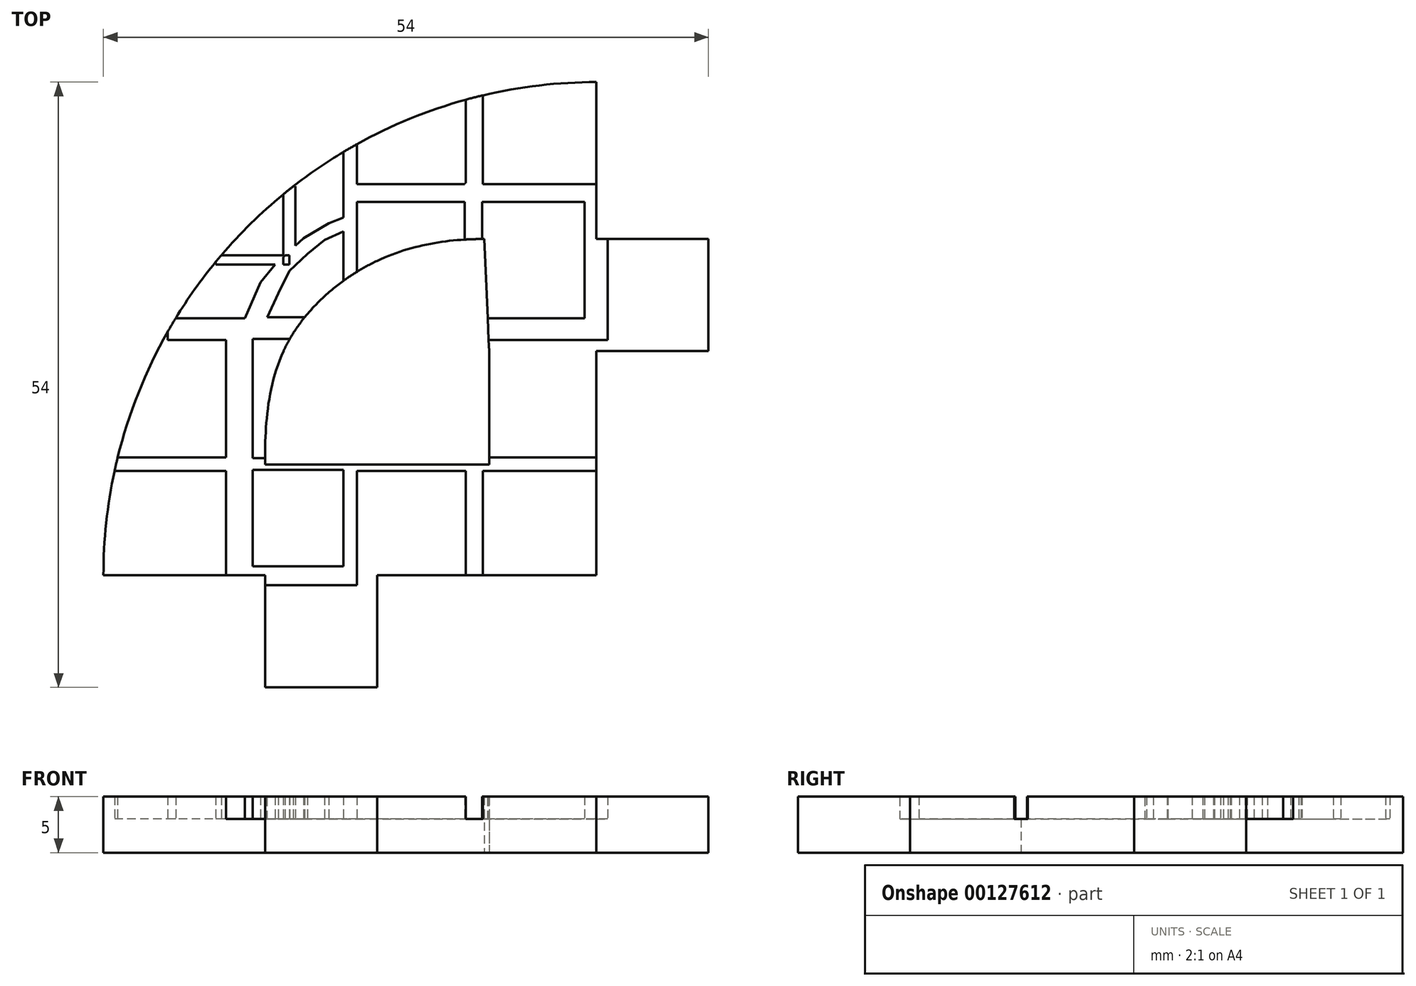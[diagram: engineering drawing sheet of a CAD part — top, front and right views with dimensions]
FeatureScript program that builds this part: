
annotation { "Feature Type Name" : "Feature", "Feature Type Description" : "" }
export const myFeature = defineFeature(function(context is Context, id is Id, definition is map)
    precondition{}
    {
        {
            var Q0;
            Q0=qCreatedBy(makeId("Top.planeOp"),FACE);
            cPlane(context, id + "F0", {"entities" : qUnion([Q0]), "cplaneType" : CPlaneType.OFFSET, "offset" : 3 * mm, "width" : 150 * mm, "height" : 150 * mm});
        }
        {
            var Q0;
            Q0=qCreatedBy(makeId("Top.planeOp"),FACE);
            var sketch = newSketch(context, id + "F1", { "sketchPlane" : qUnion([Q0])});
            skLineSegment(sketch, "E0", {"start": v(0, 0) * mm, "end": v(-19.58, 0) * mm});
            skLineSegment(sketch, "E1", {"start": v(0, 0) * mm, "end": v(0, 20) * mm});
            skLineSegment(sketch, "E2.bottom", {"start": v(0, 0) * mm, "end": v(-10, 0) * mm});
            skLineSegment(sketch, "E2.top", {"start": v(0, 9.9) * mm, "end": v(-9.58, 9.9) * mm});
            skLineSegment(sketch, "E3.bottom", {"start": v(-9.58, 9.9) * mm, "end": v(0.42, 9.9) * mm});
            skLineSegment(sketch, "E3.top", {"start": v(-9.58, 20) * mm, "end": v(0, 20) * mm});
            skLineSegment(sketch, "E3.left", {"start": v(-9.58, 9.9) * mm, "end": v(-9.58, 20) * mm});
            skLineSegment(sketch, "E4.bottom", {"start": v(-9.58, 20) * mm, "end": v(0.42, 20) * mm});
            skLineSegment(sketch, "E5.bottom", {"start": v(-9.58, 9.9) * mm, "end": v(-19.58, 9.9) * mm});
            skLineSegment(sketch, "E5.top", {"start": v(-9.58, 0) * mm, "end": v(-19.58, 0) * mm});
            skLineSegment(sketch, "E5.left", {"start": v(-9.58, 9.9) * mm, "end": v(-9.58, 0) * mm});
            skLineSegment(sketch, "E5.right", {"start": v(-19.58, 9.9) * mm, "end": v(-19.58, 0) * mm});
            skLineSegment(sketch, "E6.right", {"start": v(-29.58, 9.9) * mm, "end": v(-29.58, 0) * mm});
            skLineSegment(sketch, "E7.bottom", {"start": v(-29.58, 9.9) * mm, "end": v(-42.6, 9.9) * mm});
            skLineSegment(sketch, "E8.bottom", {"start": v(-10, 30) * mm, "end": v(0, 30) * mm});
            skLineSegment(sketch, "E9.left", {"start": v(-29.58, 0) * mm, "end": v(-29.58, -10) * mm});
            skLineSegment(sketch, "E9.right", {"start": v(-19.58, 0) * mm, "end": v(-19.58, -10) * mm});
            skLineSegment(sketch, "E10.bottom", {"start": v(0, 20) * mm, "end": v(10, 20) * mm});
            skLineSegment(sketch, "E10.top", {"start": v(0, 30) * mm, "end": v(10, 30) * mm});
            skArc(sketch, "E11", {"start": v(0, 44) * mm, "mid": v(-31.11, 31.11) * mm, "end": v(-44, 0) * mm});
            skLineSegment(sketch, "E12", {"start": v(-10, 30) * mm, "end": v(-10, 42.85) * mm});
            skLineSegment(sketch, "E13", {"start": v(-29.58, -10) * mm, "end": v(-19.58, -10) * mm});
            skLineSegment(sketch, "E14", {"start": v(-29.58, 0) * mm, "end": v(-19.58, 0) * mm});
            skLineSegment(sketch, "E15", {"start": v(-29.58, 9.9) * mm, "end": v(-19.58, 9.9) * mm});
            skLineSegment(sketch, "E16", {"start": v(0, 0) * mm, "end": v(0, 9.9) * mm});
            skLineSegment(sketch, "E17", {"start": v(-9.58, 20) * mm, "end": v(-10, 30) * mm});
            skLineSegment(sketch, "E18", {"start": v(0, 30) * mm, "end": v(0, 20) * mm});
            skLineSegment(sketch, "E19", {"start": v(10, 30) * mm, "end": v(10, 20) * mm});
            skFitSpline(sketch, "E20", {"points": [v(-29.58, 9.9) * mm, v(-27.93, 20) * mm, v(-19.58, 28.05) * mm, v(-10, 30) * mm], "startDerivative": vector(-0.16, 25.5) * mm, "endDerivative": vector(29.05, 0) * mm});
            skLineSegment(sketch, "E21", {"start": v(-19.58, 9.9) * mm, "end": v(-19.58, 28.05) * mm});
            skLineSegment(sketch, "E22", {"start": v(-9.58, 20) * mm, "end": v(-27.93, 20) * mm});
            skLineSegment(sketch, "E23", {"start": v(-27.93, 20) * mm, "end": v(-39.2, 20) * mm});
            skLineSegment(sketch, "E24", {"start": v(-19.58, 28.05) * mm, "end": v(-19.58, 39.4) * mm});
            skLineSegment(sketch, "E25", {"start": v(0, 44) * mm, "end": v(0, 30) * mm});
            skLineSegment(sketch, "E26", {"start": v(-44, 0) * mm, "end": v(-29.58, 0) * mm});
            skLineSegment(sketch, "E27", {"start": v(-33.93, 28) * mm, "end": v(-24.58, 24.6) * mm});
            skPoint(sketch, "E27.endSnap0", {"position": v(-24.58, 0) * mm});
            skLineSegment(sketch, "E28", {"start": v(-24.58, 24.6) * mm, "end": v(-27.98, 33.96) * mm});
            skLineSegment(sketch, "E29", {"start": v(-29.58, 9.9) * mm, "end": v(-24.58, 24.6) * mm, "construction": true});
            skLineSegment(sketch, "E30", {"start": v(-10, 30) * mm, "end": v(-24.58, 24.6) * mm, "construction": true});
            skSolve(sketch);
        }
        {
            var Q0;
            Q0 = qSketchRegion(id + "F1", true);
            var Q1;
            {var subQ0=sQuery(id+"F1.wireOp",EDGE,"ekZmYGLB-jqZX-6x8J-CA2y-MRHvwaimWM1N.bottom");Q1=makeQuery(id+"F1.imprint","IMPRINT",FACE,{"disambiguationData":[TD([[makeQuery(id+"F1.imprint","IMPRINT",EDGE,{"derivedFrom":subQ0}),1.0]])]});}
            var Q2;
            Q2=makeQuery(id+"F1.imprint","IMPRINT",FACE,{"disambiguationData":[TD([[makeQuery(id+"F1.imprint","IMPRINT",EDGE,{"derivedFrom":sQuery(id+"F1.wireOp",EDGE,"LGzSSFG5-AHb3-na1S-sf8x-pvlMwqtWAyyH.bottom")}),1.0]])]});
            var Q3;
            Q3=makeQuery(id+"F1.imprint","IMPRINT",FACE,{"disambiguationData":[TD([[makeQuery(id+"F1.imprint","IMPRINT",EDGE,{"derivedFrom":sQuery(id+"F1.wireOp",EDGE,"sXpVq7aK-24pz-09u2-ev60-LyjVWQO6ttF5.bottom")}),1.0]])]});
            var Q4;
            Q4=makeQuery(id+"F1.imprint","IMPRINT",FACE,{"disambiguationData":[TD([[makeQuery(id+"F1.imprint","IMPRINT",EDGE,{"derivedFrom":sQuery(id+"F1.wireOp",EDGE,"ivGXcJoi-03Uq-7aqn-IO81-W6c1Jl31SRKL.bottom")}),1.0]])]});
            extrude(context, id + "F2", {"entities" : qUnion([Q0, Q1, Q2, Q3, Q4]), "depth" : 5 * mm});
        }
        {
            var Q0;
            Q0=qCreatedBy(id+"F0.planeOp",FACE);
            var sketch = newSketch(context, id + "F3", { "sketchPlane" : qUnion([Q0])});
            skLineSegment(sketch, "E31", {"start": v(-33.07, 0) * mm, "end": v(-33.07, 22.94) * mm});
            skLineSegment(sketch, "E32", {"start": v(-33.07, 22.94) * mm, "end": v(-30.69, 22.94) * mm});
            skLineSegment(sketch, "E33", {"start": v(-30.69, 22.94) * mm, "end": v(-30.69, 0) * mm});
            skLineSegment(sketch, "E34", {"start": v(-30.69, 0) * mm, "end": v(-33.07, 0) * mm});
            skLineSegment(sketch, "E35.bottom", {"start": v(-22.58, 0) * mm, "end": v(-21.39, 0) * mm});
            skLineSegment(sketch, "E35.top", {"start": v(-22.58, 38.74) * mm, "end": v(-21.39, 38.74) * mm});
            skLineSegment(sketch, "E35.left", {"start": v(-22.58, 0) * mm, "end": v(-22.58, 38.74) * mm});
            skLineSegment(sketch, "E35.right", {"start": v(-21.39, 0) * mm, "end": v(-21.39, 38.74) * mm});
            skLineSegment(sketch, "E36.bottom", {"start": v(-11.65, 0) * mm, "end": v(-10.13, 0) * mm});
            skLineSegment(sketch, "E36.top", {"start": v(-11.65, 43.5) * mm, "end": v(-10.13, 43.5) * mm});
            skLineSegment(sketch, "E36.left", {"start": v(-11.65, 0) * mm, "end": v(-11.65, 43.5) * mm});
            skLineSegment(sketch, "E36.right", {"start": v(-10.13, 0) * mm, "end": v(-10.13, 43.5) * mm});
            skLineSegment(sketch, "E37.bottom", {"start": v(0, 9.3) * mm, "end": v(-43.24, 9.3) * mm});
            skLineSegment(sketch, "E37.top", {"start": v(0, 10.5) * mm, "end": v(-43.24, 10.5) * mm});
            skLineSegment(sketch, "E37.left", {"start": v(0, 9.3) * mm, "end": v(0, 10.5) * mm});
            skLineSegment(sketch, "E37.right", {"start": v(-43.24, 9.3) * mm, "end": v(-43.24, 10.5) * mm});
            skPoint(sketch, "E38.oppositeSnap0", {"position": v(-31.88, 22.94) * mm});
            skLineSegment(sketch, "E38.bottom", {"start": v(0, 21) * mm, "end": v(-38.26, 21) * mm});
            skLineSegment(sketch, "E38.top", {"start": v(0, 22.94) * mm, "end": v(-38.26, 22.94) * mm});
            skLineSegment(sketch, "E38.left", {"start": v(0, 21) * mm, "end": v(0, 22.94) * mm});
            skLineSegment(sketch, "E38.right", {"start": v(-38.26, 21) * mm, "end": v(-38.26, 22.94) * mm});
            skLineSegment(sketch, "E39.bottom", {"start": v(-1.04, 22.94) * mm, "end": v(1.01, 22.94) * mm});
            skLineSegment(sketch, "E39.top", {"start": v(-1.04, 34.2) * mm, "end": v(1.01, 34.2) * mm});
            skLineSegment(sketch, "E39.left", {"start": v(-1.04, 22.94) * mm, "end": v(-1.04, 34.2) * mm});
            skLineSegment(sketch, "E39.right", {"start": v(1.01, 22.94) * mm, "end": v(1.01, 34.2) * mm});
            skLineSegment(sketch, "E40.bottom", {"start": v(1.01, 22.94) * mm, "end": v(-1.04, 22.94) * mm});
            skLineSegment(sketch, "E40.top", {"start": v(1.01, 21) * mm, "end": v(-1.04, 21) * mm});
            skLineSegment(sketch, "E40.left", {"start": v(1.01, 22.94) * mm, "end": v(1.01, 21) * mm});
            skLineSegment(sketch, "E40.right", {"start": v(-1.04, 22.94) * mm, "end": v(-1.04, 21) * mm});
            skPoint(sketch, "E41.oppositeSnap0", {"position": v(-0.02, 34.2) * mm});
            skLineSegment(sketch, "E41.bottom", {"start": v(-22.58, 34.9) * mm, "end": v(-0.02, 34.9) * mm});
            skLineSegment(sketch, "E41.top", {"start": v(-22.58, 33.3) * mm, "end": v(-0.02, 33.3) * mm});
            skLineSegment(sketch, "E41.left", {"start": v(-22.58, 34.9) * mm, "end": v(-22.58, 33.3) * mm});
            skLineSegment(sketch, "E41.right", {"start": v(-0.02, 34.9) * mm, "end": v(-0.02, 33.3) * mm});
            skLineSegment(sketch, "E42.bottom", {"start": v(-27.41, 27.71) * mm, "end": v(-33.97, 27.71) * mm});
            skLineSegment(sketch, "E42.top", {"start": v(-27.41, 28.56) * mm, "end": v(-33.97, 28.56) * mm});
            skLineSegment(sketch, "E42.left", {"start": v(-27.41, 27.71) * mm, "end": v(-27.41, 28.56) * mm});
            skLineSegment(sketch, "E42.right", {"start": v(-33.97, 27.71) * mm, "end": v(-33.97, 28.56) * mm});
            skLineSegment(sketch, "E43.bottom", {"start": v(-26.87, 27.71) * mm, "end": v(-27.96, 27.71) * mm});
            skLineSegment(sketch, "E43.top", {"start": v(-26.87, 34.7) * mm, "end": v(-27.96, 34.7) * mm});
            skLineSegment(sketch, "E43.left", {"start": v(-26.87, 27.71) * mm, "end": v(-26.87, 34.7) * mm});
            skLineSegment(sketch, "E43.right", {"start": v(-27.96, 27.71) * mm, "end": v(-27.96, 34.7) * mm});
            skLineSegment(sketch, "E44", {"start": v(-31.36, 22.94) * mm, "end": v(-29.96, 26.13) * mm});
            skLineSegment(sketch, "E45", {"start": v(-29.96, 26.13) * mm, "end": v(-28.69, 27.71) * mm});
            skLineSegment(sketch, "E46", {"start": v(-28.69, 27.71) * mm, "end": v(-26.14, 30.08) * mm});
            skLineSegment(sketch, "E47", {"start": v(-26.14, 30.08) * mm, "end": v(-23.9, 31.42) * mm});
            skLineSegment(sketch, "E48", {"start": v(-23.9, 31.42) * mm, "end": v(-22.58, 31.9) * mm});
            skLineSegment(sketch, "E49", {"start": v(-22.58, 31.9) * mm, "end": v(-22.58, 30.69) * mm});
            skLineSegment(sketch, "E50", {"start": v(-22.58, 30.69) * mm, "end": v(-24.26, 29.9) * mm});
            skLineSegment(sketch, "E51", {"start": v(-24.26, 29.9) * mm, "end": v(-25.77, 28.68) * mm});
            skLineSegment(sketch, "E52", {"start": v(-25.77, 28.68) * mm, "end": v(-27.41, 27.16) * mm});
            skLineSegment(sketch, "E53", {"start": v(-27.41, 27.16) * mm, "end": v(-28.39, 25.16) * mm});
            skLineSegment(sketch, "E54", {"start": v(-28.39, 25.16) * mm, "end": v(-29.42, 22.94) * mm});
            skPoint(sketch, "E55.firstSnap0", {"position": v(-31.88, 0) * mm});
            skLineSegment(sketch, "E55.bottom", {"start": v(-31.88, -0.88) * mm, "end": v(-21.39, -0.88) * mm});
            skLineSegment(sketch, "E55.top", {"start": v(-31.88, 0.8) * mm, "end": v(-21.39, 0.8) * mm});
            skLineSegment(sketch, "E55.left", {"start": v(-31.88, -0.88) * mm, "end": v(-31.88, 0.8) * mm});
            skLineSegment(sketch, "E55.right", {"start": v(-21.39, -0.88) * mm, "end": v(-21.39, 0.8) * mm});
            skSolve(sketch);
        }
        {
            var Q0;
            Q0 = qSketchRegion(id + "F3", true);
            extrude(context, id + "F4", {"entities" : qUnion([Q0]), "operationType" : NewBodyOperationType.REMOVE, "depth" : 25 * mm});
        }
        {
            var Q0;
            Q0=qCreatedBy(id+"F0.planeOp",FACE);
            var sketch = newSketch(context, id + "F5", { "sketchPlane" : qUnion([Q0])});
            skLineSegment(sketch, "E56.bottom", {"start": v(-30.86, 23.03) * mm, "end": v(-10.21, 23.03) * mm});
            skLineSegment(sketch, "E56.top", {"start": v(-30.86, 21.1) * mm, "end": v(-10.21, 21.1) * mm});
            skLineSegment(sketch, "E56.left", {"start": v(-30.86, 23.03) * mm, "end": v(-30.86, 21.1) * mm});
            skLineSegment(sketch, "E56.right", {"start": v(-10.21, 23.03) * mm, "end": v(-10.21, 21.1) * mm});
            skLineSegment(sketch, "E57.bottom", {"start": v(-22.76, 9.39) * mm, "end": v(-21.21, 9.39) * mm});
            skLineSegment(sketch, "E57.top", {"start": v(-22.76, 23.03) * mm, "end": v(-21.21, 23.03) * mm});
            skLineSegment(sketch, "E57.left", {"start": v(-22.76, 9.39) * mm, "end": v(-22.76, 23.03) * mm});
            skLineSegment(sketch, "E57.right", {"start": v(-21.21, 9.39) * mm, "end": v(-21.21, 23.03) * mm});
            skLineSegment(sketch, "E58.bottom", {"start": v(-11.75, 23.03) * mm, "end": v(-10.21, 23.03) * mm});
            skLineSegment(sketch, "E58.top", {"start": v(-11.75, 35) * mm, "end": v(-10.21, 35) * mm});
            skLineSegment(sketch, "E58.left", {"start": v(-11.75, 23.03) * mm, "end": v(-11.75, 35) * mm});
            skLineSegment(sketch, "E58.right", {"start": v(-10.21, 23.03) * mm, "end": v(-10.21, 35) * mm});
            skLineSegment(sketch, "E59.bottom", {"start": v(-22.76, 9.39) * mm, "end": v(-33.06, 9.39) * mm});
            skLineSegment(sketch, "E59.top", {"start": v(-22.76, 10.44) * mm, "end": v(-33.06, 10.44) * mm});
            skLineSegment(sketch, "E59.left", {"start": v(-22.76, 9.39) * mm, "end": v(-22.76, 10.44) * mm});
            skLineSegment(sketch, "E59.right", {"start": v(-33.06, 9.39) * mm, "end": v(-33.06, 10.44) * mm});
            skSolve(sketch);
        }
        {
            var Q0;
            Q0 = qSketchRegion(id + "F5", true);
            extrude(context, id + "F6", {"entities" : qUnion([Q0]), "operationType" : NewBodyOperationType.REMOVE, "depth" : 25 * mm});
        }
    });
